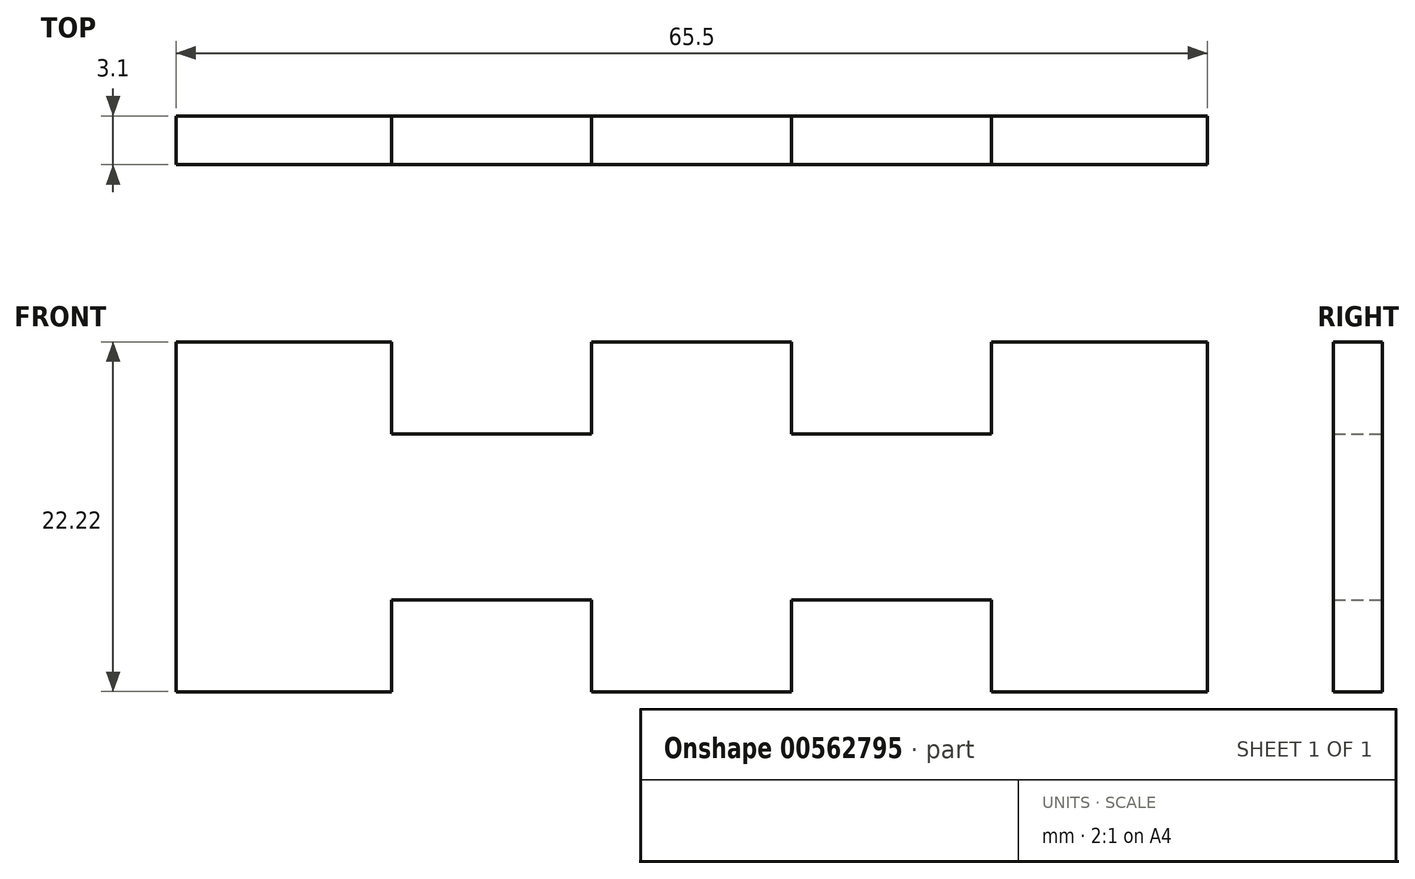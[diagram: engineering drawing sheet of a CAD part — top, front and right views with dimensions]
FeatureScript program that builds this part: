
annotation { "Feature Type Name" : "Feature", "Feature Type Description" : "" }
export const myFeature = defineFeature(function(context is Context, id is Id, definition is map)
    precondition{}
    {
        {
            var Q0;
            Q0=qCreatedBy(makeId("Front.planeOp"),FACE);
            var sketch = newSketch(context, id + "F0", { "sketchPlane" : qUnion([Q0])});
            skLineSegment(sketch, "E0.bottom", {"start": v(-31.75, 11.11) * mm, "end": v(-19.05, 11.11) * mm});
            skLineSegment(sketch, "E0.top", {"start": v(-31.75, -11.11) * mm, "end": v(-19.05, -11.11) * mm});
            skPoint(sketch, "E0.middle", {"position": v(0, 0) * mm});
            skLineSegment(sketch, "E1.bottom", {"start": v(-6.35, 5.27) * mm, "end": v(-19.05, 5.27) * mm});
            skLineSegment(sketch, "E1.left", {"start": v(-6.35, 5.27) * mm, "end": v(-6.35, 11.11) * mm});
            skLineSegment(sketch, "E1.right", {"start": v(-19.05, 5.27) * mm, "end": v(-19.05, 11.11) * mm});
            skPoint(sketch, "E1.middle", {"position": v(-12.7, 8.2) * mm});
            skLineSegment(sketch, "E2.trimOffspring", {"start": v(-6.35, 11.11) * mm, "end": v(6.35, 11.11) * mm});
            skLineSegment(sketch, "E3.MirrorCS", {"start": v(31.75, 11.11) * mm, "end": v(19.05, 11.11) * mm});
            skLineSegment(sketch, "E4.MirrorCS", {"start": v(6.35, 5.27) * mm, "end": v(19.05, 5.27) * mm});
            skLineSegment(sketch, "E5.MirrorCS", {"start": v(6.35, 11.11) * mm, "end": v(-6.35, 11.11) * mm});
            skLineSegment(sketch, "E6.MirrorCS", {"start": v(19.05, 5.27) * mm, "end": v(19.05, 11.11) * mm});
            skLineSegment(sketch, "E7.MirrorCS", {"start": v(6.35, 5.27) * mm, "end": v(6.35, 11.11) * mm});
            skPoint(sketch, "E8.MirrorP", {"position": v(12.7, 8.2) * mm});
            skLineSegment(sketch, "E9.trimOffspring", {"start": v(-19.05, 11.11) * mm, "end": v(-31.75, 11.11) * mm});
            skLineSegment(sketch, "E10.trimOffspring", {"start": v(19.05, 11.11) * mm, "end": v(31.75, 11.11) * mm});
            skLineSegment(sketch, "E11.MirrorCS", {"start": v(31.75, -11.11) * mm, "end": v(19.05, -11.11) * mm});
            skLineSegment(sketch, "E12.MirrorCS", {"start": v(-6.35, -11.11) * mm, "end": v(6.35, -11.11) * mm});
            skLineSegment(sketch, "E13.MirrorCS", {"start": v(19.05, -11.11) * mm, "end": v(31.75, -11.11) * mm});
            skLineSegment(sketch, "E14.MirrorCS", {"start": v(-19.05, -11.11) * mm, "end": v(-31.75, -11.11) * mm});
            skLineSegment(sketch, "E15.MirrorCS", {"start": v(6.35, -5.27) * mm, "end": v(6.35, -11.11) * mm});
            skLineSegment(sketch, "E16.MirrorCS", {"start": v(19.05, -5.27) * mm, "end": v(19.05, -11.11) * mm});
            skLineSegment(sketch, "E17.MirrorCS", {"start": v(6.35, -11.11) * mm, "end": v(-6.35, -11.11) * mm});
            skLineSegment(sketch, "E18.MirrorCS", {"start": v(6.35, -5.27) * mm, "end": v(19.05, -5.27) * mm});
            skLineSegment(sketch, "E19.MirrorCS", {"start": v(-19.05, -5.27) * mm, "end": v(-19.05, -11.11) * mm});
            skPoint(sketch, "E20.MirrorP", {"position": v(12.7, -8.2) * mm});
            skPoint(sketch, "E21.MirrorP", {"position": v(-12.7, -8.2) * mm});
            skLineSegment(sketch, "E22.MirrorCS", {"start": v(-6.35, -5.27) * mm, "end": v(-19.05, -5.27) * mm});
            skLineSegment(sketch, "E23.MirrorCS", {"start": v(-6.35, -5.27) * mm, "end": v(-6.35, -11.11) * mm});
            skLineSegment(sketch, "E24.bottom", {"start": v(-31.75, 11.11) * mm, "end": v(-32.75, 11.11) * mm});
            skLineSegment(sketch, "E24.top", {"start": v(-31.75, -11.11) * mm, "end": v(-32.75, -11.11) * mm});
            skLineSegment(sketch, "E24.right", {"start": v(-32.75, 11.11) * mm, "end": v(-32.75, -11.11) * mm});
            skLineSegment(sketch, "E25.MirrorCS", {"start": v(31.75, -11.11) * mm, "end": v(32.75, -11.11) * mm});
            skLineSegment(sketch, "E26.MirrorCS", {"start": v(31.75, 11.11) * mm, "end": v(32.75, 11.11) * mm});
            skLineSegment(sketch, "E27.MirrorCS", {"start": v(32.75, 11.11) * mm, "end": v(32.75, -11.11) * mm});
            skPoint(sketch, "E28.MirrorCS.end.orphan", {"position": v(31.75, -11.11) * mm});
            skPoint(sketch, "E28.MirrorCS.start.orphan", {"position": v(31.75, 11.11) * mm});
            skSolve(sketch);
        }
        {
            var Q0;
            Q0 = qSketchRegion(id + "F0", true);
            extrude(context, id + "F1", {"entities" : qUnion([Q0]), "depth" : 3.1 * mm, "offsetDistance" : 25.4 * mm});
        }
    });
